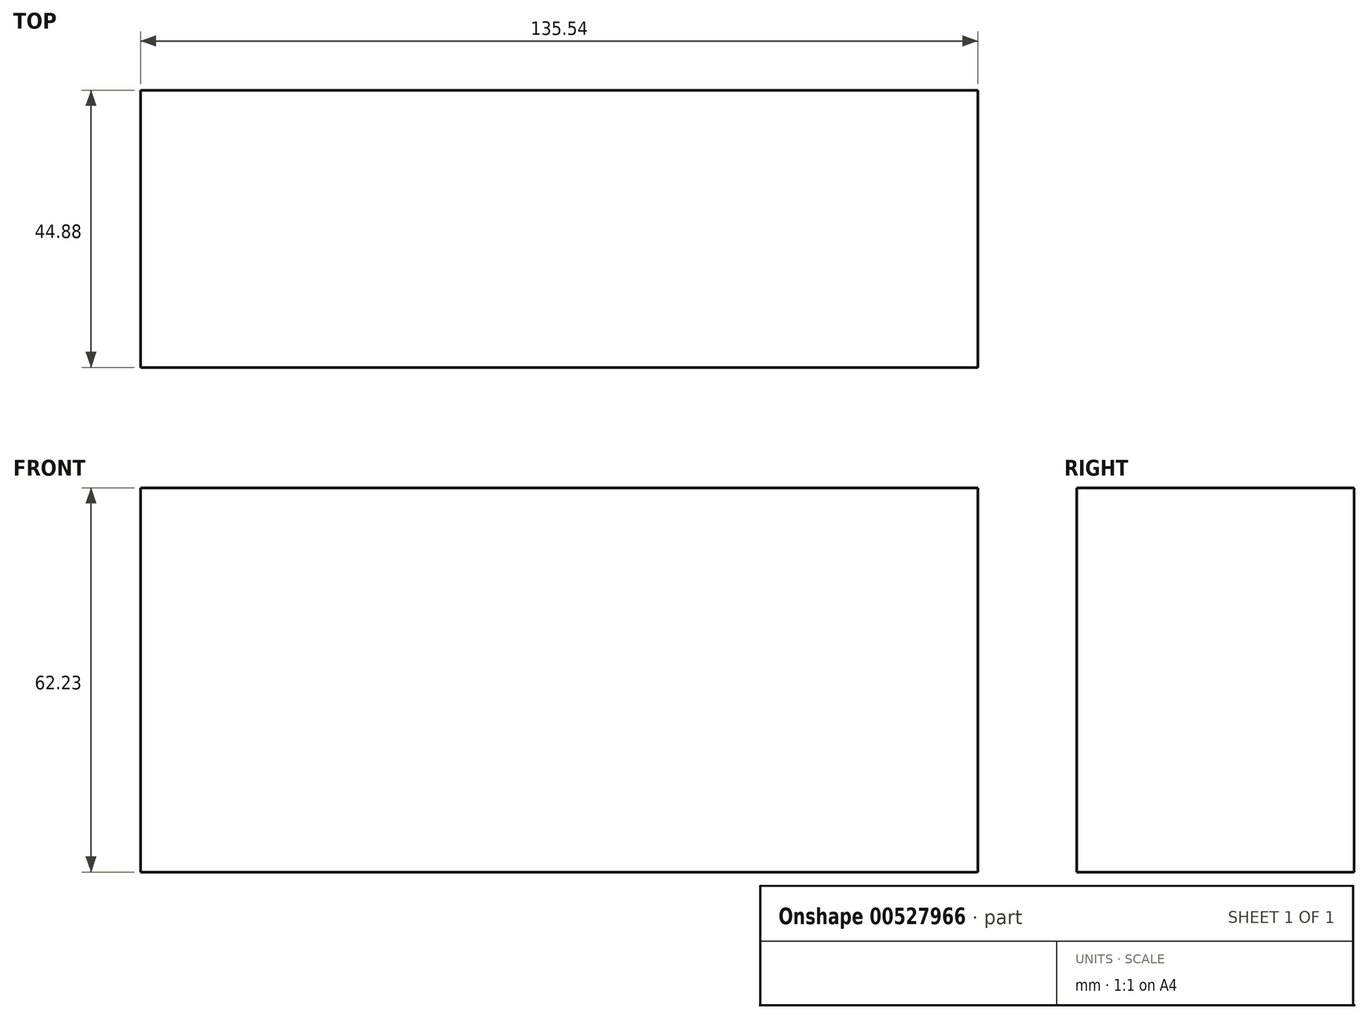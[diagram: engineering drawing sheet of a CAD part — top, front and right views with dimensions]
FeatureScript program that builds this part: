
annotation { "Feature Type Name" : "Feature", "Feature Type Description" : "" }
export const myFeature = defineFeature(function(context is Context, id is Id, definition is map)
    precondition{}
    {
        {
            var Q0;
            Q0=qCreatedBy(makeId("Top.planeOp"),FACE);
            var sketch = newSketch(context, id + "F0", { "sketchPlane" : qUnion([Q0])});
            skLineSegment(sketch, "E0.bottom", {"start": v(-59.96, 0) * mm, "end": v(75.58, 0) * mm});
            skLineSegment(sketch, "E0.top", {"start": v(-59.96, -44.88) * mm, "end": v(75.58, -44.88) * mm});
            skLineSegment(sketch, "E0.left", {"start": v(-59.96, 0) * mm, "end": v(-59.96, -44.88) * mm});
            skLineSegment(sketch, "E0.right", {"start": v(75.58, 0) * mm, "end": v(75.58, -44.88) * mm});
            skSolve(sketch);
        }
        {
            var Q0;
            Q0=makeQuery(id+"F0.imprint","IMPRINT",FACE,{"disambiguationData":[TD([[makeQuery(id+"F0.imprint","IMPRINT",EDGE,{"derivedFrom":sQuery(id+"F0.wireOp",EDGE,"E0.bottom")}),-1.0]])]});
            extrude(context, id + "F1", {"entities" : qUnion([Q0]), "depth" : 62.23 * mm, "offsetDistance" : 25.4 * mm});
        }
    });
